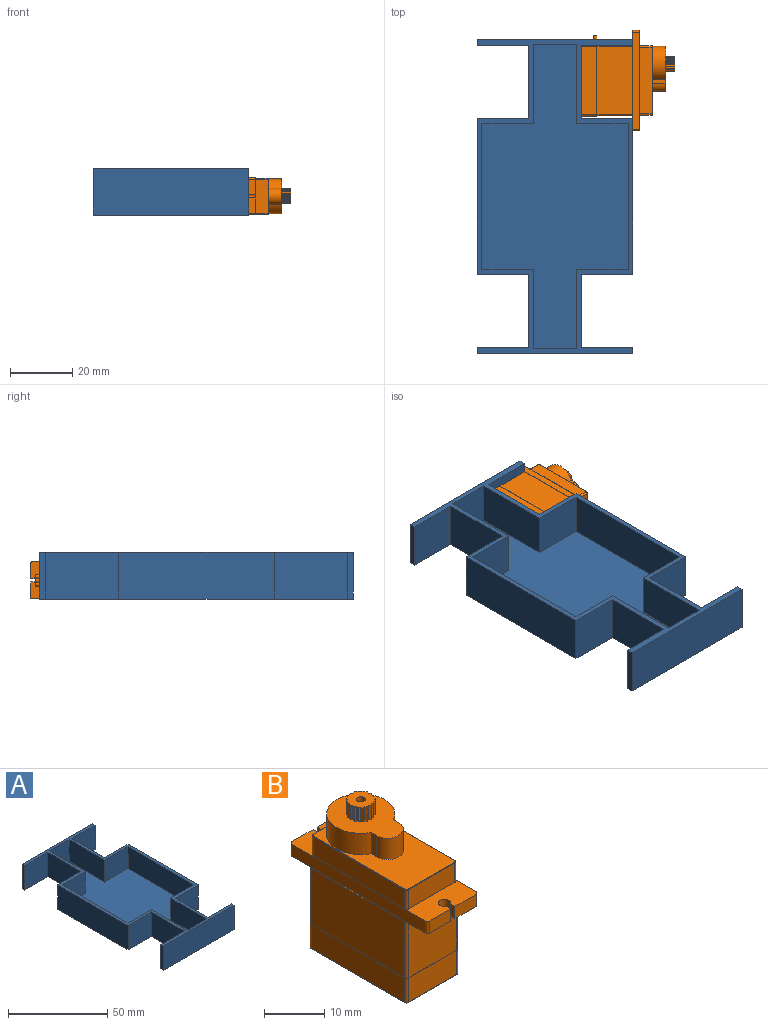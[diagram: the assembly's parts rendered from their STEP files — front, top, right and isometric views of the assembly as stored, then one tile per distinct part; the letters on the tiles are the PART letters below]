
ASSEMBLY  parts=2 mates=1
PART A: 35 faces, bbox 50x101x15 mm
  f0: plane 16.5x15mm, normal (0,1,0), area 247.5mm2, adj f1,f19,f20,f21
  f1: plane 50x15mm, normal (-1,0,0), area 750mm2, adj f0,f2,f20,f21
  f2: plane 16.5x15mm, normal (0,-1,0), area 247.5mm2, adj f1,f3,f20,f21
  f3: plane 23.5x15mm, normal (-1,0,0), area 352.5mm2, adj f2,f4,f20,f21
  f4: plane 16.5x15mm, normal (0,1,0), area 247.5mm2, adj f3,f5,f20,f21
  f5: plane 15x2mm, normal (-1,0,0), area 30mm2, adj f4,f6,f20,f21
  f6: plane 50x15mm, normal (0,-1,0), area 750mm2, adj f5,f7,f20,f21
  f7: plane 15x2mm, normal (1,0,0), area 30mm2, adj f6,f8,f20,f21
  f8: plane 16.5x15mm, normal (0,1,0), area 247.5mm2, adj f7,f9,f20,f21
  f9: plane 23.5x15mm, normal (1,0,0), area 352.5mm2, adj f8,f10,f20,f21
  f10: plane 16.5x15mm, normal (0,-1,0), area 247.5mm2, adj f9,f11,f20,f21
  f11: plane 50x15mm, normal (1,0,0), area 750mm2, adj f10,f12,f20,f21
  f12: plane 16.5x15mm, normal (0,1,0), area 247.5mm2, adj f11,f13,f20,f21
  f13: plane 23.5x15mm, normal (1,0,0), area 352.5mm2, adj f12,f14,f20,f21
  f14: plane 16.5x15mm, normal (0,-1,0), area 247.5mm2, adj f13,f15,f20,f21
  f15: plane 15x2mm, normal (1,0,0), area 30mm2, adj f14,f16,f20,f21
  f16: plane 50x15mm, normal (0,1,0), area 750mm2, adj f15,f17,f20,f21
  f17: plane 15x2mm, normal (-1,0,0), area 30mm2, adj f16,f18,f20,f21
  f18: plane 16.5x15mm, normal (0,-1,0), area 247.5mm2, adj f17,f19,f20,f21
  f19: plane 23.5x15mm, normal (-1,0,0), area 352.5mm2, adj f0,f18,f20,f21
  f20: plane 101x50mm, normal (0,0,1), area 576mm2, adj f0,f1,f2,f3,f4,f5,f6,f7
  f21: plane 101x50mm, normal (0,0,-1), area 3499mm2, adj f0,f1,f2,f3,f4,f5,f6,f7
  f22: plane 16.5x13.5mm, normal (0,-1,0), area 222.7mm2, adj f20,f23,f33,f34
  f23: plane 47x13.5mm, normal (1,0,0), area 634.5mm2, adj f20,f22,f24,f34
  f24: plane 16.5x13.5mm, normal (0,1,0), area 222.8mm2, adj f20,f23,f25,f34
  f25: plane 25.5x13.5mm, normal (1,0,0), area 344.2mm2, adj f20,f24,f26,f34
  f26: plane 14x13.5mm, normal (0,1,0), area 189mm2, adj f20,f25,f27,f34
  f27: plane 25.5x13.5mm, normal (-1,0,0), area 344.3mm2, adj f20,f26,f28,f34
  f28: plane 16.5x13.5mm, normal (0,1,0), area 222.8mm2, adj f20,f27,f29,f34
  f29: plane 47x13.5mm, normal (-1,0,0), area 634.5mm2, adj f20,f28,f30,f34
  f30: plane 16.5x13.5mm, normal (0,-1,0), area 222.7mm2, adj f20,f29,f31,f34
  f31: plane 25.5x13.5mm, normal (-1,0,0), area 344.3mm2, adj f20,f30,f32,f34
  f32: plane 14x13.5mm, normal (0,-1,0), area 189mm2, adj f20,f31,f33,f34
  f33: plane 25.5x13.5mm, normal (1,0,0), area 344.3mm2, adj f20,f22,f32,f34
  f34: plane 98x47mm, normal (0,0,1), area 2923mm2, adj f22,f23,f24,f25,f26,f27,f28,f29
PART B: 118 faces, bbox 12.4x32.3x30 mm
  f0: cylinder r=0.6mm len=3mm, axis (0,-1,0), area 11.3mm2, adj f15,f117
  f1: cylinder r=0.6mm len=3mm, axis (0,-1,0), area 11.3mm2, adj f15,f116
  f2: cylinder r=0.6mm len=3mm, axis (0,-1,0), area 11.3mm2, adj f15,f115
  f3: cylinder r=0.75mm len=2.9mm, axis (0,0,-1), area 13.7mm2, adj f97,f98
  f4: cylinder r=5.65mm len=11.3mm, axis (0,0,-1), area 129.4mm2, adj f6,f53,f54,f55
  f5: cylinder r=1mm len=2.45mm, axis (0,0,-1), area 12.8mm2, adj f7,f29,f42,f43
  f6: plane 14.55x11.3mm, normal (0,0,1), area 98.5mm2, adj f4,f54,f55,f56,f57,f58,f59,f60
  f7: plane 32.25x11.9mm, normal (0,0,1), area 111.1mm2, adj f5,f30,f31,f32,f33,f34,f35,f36
  f8: plane 22.41x0.15mm, normal (0,0,1), area 3.3mm2, adj f23,f24,f25,f39
  f9: plane 22.85x12.3mm, normal (0,0,1), area 4.1mm2, adj f10,f11,f12,f13,f14,f15,f16,f17
  f10: cylinder r=0.5mm len=4.9mm, axis (0,0,-1), area 3.8mm2, adj f9,f11,f17,f112
  f11: plane 11.3x4.9mm, normal (0,-1,0), area 55.4mm2, adj f9,f10,f12,f114
  f12: cylinder r=0.5mm len=4.9mm, axis (0,0,-1), area 3.8mm2, adj f9,f11,f13,f113
  f13: plane 21.85x4.9mm, normal (1,0,0), area 107.1mm2, adj f9,f12,f14,f111
  f14: cylinder r=0.5mm len=4.9mm, axis (0,0,-1), area 3.8mm2, adj f9,f13,f15,f109
  f15: plane 11.3x4.9mm, normal (0,1,0), area 52mm2, adj f0,f1,f2,f9,f14,f16,f107
  f16: cylinder r=0.5mm len=4.9mm, axis (0,0,-1), area 3.8mm2, adj f9,f15,f17,f108
  f17: plane 21.85x4.9mm, normal (-1,0,0), area 107.1mm2, adj f9,f10,f16,f110
  f18: plane 22.65x12.1mm, normal (0,0,-1), area 273.9mm2, adj f107,f108,f109,f110,f111,f112,f113,f114
  f19: cylinder r=0.5mm len=11.35mm, axis (0,0,-1), area 8.9mm2, adj f9,f20,f26,f27,f29
  f20: plane 21.7x11.35mm, normal (1,0,0), area 246.3mm2, adj f9,f19,f21,f27
  f21: cylinder r=0.5mm len=11.35mm, axis (0,0,-1), area 8.9mm2, adj f9,f20,f22,f27,f28
  f22: plane 11.35x11.2mm, normal (0,1,0), area 127.1mm2, adj f9,f21,f23,f28
  f23: cylinder r=0.5mm len=11.35mm, axis (0,0,-1), area 8.9mm2, adj f8,f9,f22,f24,f28
  f24: plane 21.7x11.35mm, normal (-1,0,0), area 246.3mm2, adj f8,f9,f23,f25
  f25: cylinder r=0.5mm len=11.35mm, axis (0,0,-1), area 8.9mm2, adj f8,f9,f24,f26,f29
  f26: plane 11.35x11.2mm, normal (0,-1,0), area 127.1mm2, adj f9,f19,f25,f29
  f27: plane 22.41x0.15mm, normal (0,0,1), area 3.3mm2, adj f19,f20,f21,f31
  f28: plane 11.9x4.92mm, normal (0,0,-1), area 52.6mm2, adj f21,f22,f23,f31,f32,f33,f34,f35
  f29: plane 11.9x4.92mm, normal (0,0,-1), area 52.6mm2, adj f5,f19,f25,f26,f30,f31,f39,f40
  f30: cylinder r=0.5mm len=2.45mm, axis (0,0,-1), area 1.9mm2, adj f7,f29,f31,f44
  f31: plane 31.25x2.45mm, normal (1,0,0), area 76.6mm2, adj f7,f27,f28,f29,f30,f32
  f32: cylinder r=0.5mm len=2.45mm, axis (0,0,-1), area 1.9mm2, adj f7,f28,f31,f33
  f33: plane 4.95x2.45mm, normal (0,1,0), area 12.1mm2, adj f7,f28,f32,f34
  f34: plane 2.45x1.13mm, normal (-1,0,0), area 2.8mm2, adj f7,f28,f33,f35
  f35: cylinder r=1mm len=2.45mm, axis (0,0,-1), area 12.8mm2, adj f7,f28,f34,f36
  f36: plane 2.45x1.13mm, normal (1,0,0), area 2.8mm2, adj f7,f28,f35,f37
  f37: plane 4.95x2.45mm, normal (0,1,0), area 12.1mm2, adj f7,f28,f36,f38
  f38: cylinder r=0.5mm len=2.45mm, axis (0,0,-1), area 1.9mm2, adj f7,f28,f37,f39
  f39: plane 31.25x2.45mm, normal (-1,0,0), area 76.6mm2, adj f7,f8,f28,f29,f38,f40
  f40: cylinder r=0.5mm len=2.45mm, axis (0,0,-1), area 1.9mm2, adj f7,f29,f39,f41
  f41: plane 4.95x2.45mm, normal (0,-1,0), area 12.1mm2, adj f7,f29,f40,f42
  f42: plane 2.45x1.13mm, normal (1,0,0), area 2.8mm2, adj f5,f7,f29,f41
  f43: plane 2.45x1.13mm, normal (-1,0,0), area 2.8mm2, adj f5,f7,f29,f44
  f44: plane 4.95x2.45mm, normal (0,-1,0), area 12.1mm2, adj f7,f29,f30,f43
  f45: cylinder r=0.5mm len=3.9mm, axis (0,0,-1), area 3.1mm2, adj f7,f46,f52,f99
  f46: plane 21.4x3.9mm, normal (1,0,0), area 83.5mm2, adj f7,f45,f47,f100
  f47: cylinder r=0.5mm len=3.9mm, axis (0,0,-1), area 3.1mm2, adj f7,f46,f48,f102
  f48: plane 10.8x3.9mm, normal (0,1,0), area 42.1mm2, adj f7,f47,f49,f104
  f49: cylinder r=0.5mm len=3.9mm, axis (0,0,-1), area 3.1mm2, adj f7,f48,f50,f106
  f50: plane 21.4x3.9mm, normal (-1,0,0), area 83.5mm2, adj f7,f49,f51,f105
  f51: cylinder r=0.5mm len=3.9mm, axis (0,0,-1), area 3.1mm2, adj f7,f50,f52,f103
  f52: plane 10.8x3.9mm, normal (0,-1,0), area 42.1mm2, adj f7,f45,f51,f101
  f53: plane 22.2x11.6mm, normal (0,0,1), area 142mm2, adj f4,f54,f55,f56,f99,f100,f101,f102
  f54: plane 4.3x1.28mm, normal (1,0,0), area 5.5mm2, adj f4,f6,f53,f56
  f55: plane 4.3x1.28mm, normal (-1,0,0), area 5.5mm2, adj f4,f6,f53,f56
  f56: cylinder r=2.6mm len=5.2mm, axis (0,0,-1), area 35.1mm2, adj f6,f53,f54,f55
  f57: plane 2.9x0.32mm, normal (0.63,0.78,0), area 1.2mm2, adj f6,f58,f96,f97
  f58: plane 2.9x0.42mm, normal (1,0.05,0), area 1.2mm2, adj f6,f57,f59,f97
  f59: plane 2.9x0.39mm, normal (0.36,0.93,0), area 1.2mm2, adj f6,f58,f60,f97
  f60: plane 2.9x0.39mm, normal (0.93,0.36,0), area 1.2mm2, adj f6,f59,f61,f97
  f61: plane 2.9x0.42mm, normal (0.05,1,0), area 1.2mm2, adj f6,f60,f62,f97
  f62: plane 2.9x0.32mm, normal (0.78,0.63,0), area 1.2mm2, adj f6,f61,f63,f97
  f63: plane 2.9x0.4mm, normal (-0.26,0.97,0), area 1.2mm2, adj f6,f62,f64,f97
  f64: plane 2.9x0.35mm, normal (0.55,0.84,0), area 1.2mm2, adj f6,f63,f65,f97
  f65: plane 2.9x0.35mm, normal (-0.55,0.84,0), area 1.2mm2, adj f6,f64,f66,f97
  f66: plane 2.9x0.4mm, normal (0.26,0.97,0), area 1.2mm2, adj f6,f65,f67,f97
  f67: plane 2.9x0.32mm, normal (-0.78,0.63,0), area 1.2mm2, adj f6,f66,f68,f97
  f68: plane 2.9x0.42mm, normal (-0.05,1,0), area 1.2mm2, adj f6,f67,f69,f97
  f69: plane 2.9x0.39mm, normal (-0.93,0.36,0), area 1.2mm2, adj f6,f68,f70,f97
  f70: plane 2.9x0.39mm, normal (-0.36,0.93,0), area 1.2mm2, adj f6,f69,f71,f97
  f71: plane 2.9x0.42mm, normal (-1,0.05,0), area 1.2mm2, adj f6,f70,f72,f97
  f72: plane 2.9x0.32mm, normal (-0.63,0.78,0), area 1.2mm2, adj f6,f71,f73,f97
  f73: plane 2.9x0.4mm, normal (-0.97,-0.26,0), area 1.2mm2, adj f6,f72,f74,f97
  f74: plane 2.9x0.35mm, normal (-0.84,0.55,0), area 1.2mm2, adj f6,f73,f75,f97
  f75: plane 2.9x0.35mm, normal (-0.84,-0.55,0), area 1.2mm2, adj f6,f74,f76,f97
  f76: plane 2.9x0.4mm, normal (-0.97,0.26,0), area 1.2mm2, adj f6,f75,f77,f97
  f77: plane 2.9x0.32mm, normal (-0.63,-0.78,0), area 1.2mm2, adj f6,f76,f78,f97
  f78: plane 2.9x0.42mm, normal (-1,-0.05,0), area 1.2mm2, adj f6,f77,f79,f97
  f79: plane 2.9x0.39mm, normal (-0.36,-0.93,0), area 1.2mm2, adj f6,f78,f80,f97
  f80: plane 2.9x0.39mm, normal (-0.93,-0.36,0), area 1.2mm2, adj f6,f79,f81,f97
  f81: plane 2.9x0.42mm, normal (-0.05,-1,0), area 1.2mm2, adj f6,f80,f82,f97
  f82: plane 2.9x0.32mm, normal (-0.78,-0.63,0), area 1.2mm2, adj f6,f81,f83,f97
  f83: plane 2.9x0.4mm, normal (0.26,-0.97,0), area 1.2mm2, adj f6,f82,f84,f97
  f84: plane 2.9x0.35mm, normal (-0.55,-0.84,0), area 1.2mm2, adj f6,f83,f85,f97
  f85: plane 2.9x0.35mm, normal (0.55,-0.84,0), area 1.2mm2, adj f6,f84,f86,f97
  f86: plane 2.9x0.4mm, normal (-0.26,-0.97,0), area 1.2mm2, adj f6,f85,f87,f97
  f87: plane 2.9x0.32mm, normal (0.78,-0.63,0), area 1.2mm2, adj f6,f86,f88,f97
  f88: plane 2.9x0.42mm, normal (0.05,-1,0), area 1.2mm2, adj f6,f87,f89,f97
  f89: plane 2.9x0.39mm, normal (0.93,-0.36,0), area 1.2mm2, adj f6,f88,f90,f97
  f90: plane 2.9x0.39mm, normal (0.36,-0.93,0), area 1.2mm2, adj f6,f89,f91,f97
  f91: plane 2.9x0.42mm, normal (1,-0.05,0), area 1.2mm2, adj f6,f90,f92,f97
  f92: plane 2.9x0.32mm, normal (0.63,-0.78,0), area 1.2mm2, adj f6,f91,f93,f97
  f93: plane 2.9x0.4mm, normal (0.97,0.26,0), area 1.2mm2, adj f6,f92,f94,f97
  f94: plane 2.9x0.35mm, normal (0.84,-0.55,0), area 1.2mm2, adj f6,f93,f95,f97
  f95: plane 2.9x0.35mm, normal (0.84,0.55,0), area 1.2mm2, adj f6,f94,f96,f97
  f96: plane 2.9x0.4mm, normal (0.97,-0.26,0), area 1.2mm2, adj f6,f57,f95,f97
  f97: plane 4.85x4.85mm, normal (0,0,1), area 15.1mm2, adj f3,f57,f58,f59,f60,f61,f62,f63
  f98: plane 1.5x1.5mm, normal (0,0,1), area 1.8mm2, adj f3
  f99: torus R=0.4mm, axis (0,0,1), area 0.1mm2, adj f45,f53,f100,f101
  f100: cylinder r=0.1mm len=21.4mm, axis (0,-1,0), area 3.4mm2, adj f46,f53,f99,f102
  f101: cylinder r=0.1mm len=10.8mm, axis (-1,0,0), area 1.7mm2, adj f52,f53,f99,f103
  f102: torus R=0.4mm, axis (0,0,1), area 0.1mm2, adj f47,f53,f100,f104
  f103: torus R=0.4mm, axis (0,0,1), area 0.1mm2, adj f51,f53,f101,f105
  f104: cylinder r=0.1mm len=10.8mm, axis (1,0,0), area 1.7mm2, adj f48,f53,f102,f106
  f105: cylinder r=0.1mm len=21.4mm, axis (0,1,0), area 3.4mm2, adj f50,f53,f103,f106
  f106: torus R=0.4mm, axis (0,0,1), area 0.1mm2, adj f49,f53,f104,f105
  f107: cylinder r=0.1mm len=11.3mm, axis (1,0,0), area 1.8mm2, adj f15,f18,f108,f109
  f108: torus R=0.4mm, axis (0,0,-1), area 0.1mm2, adj f16,f18,f107,f110
  f109: torus R=0.4mm, axis (0,0,-1), area 0.1mm2, adj f14,f18,f107,f111
  f110: cylinder r=0.1mm len=21.85mm, axis (0,1,0), area 3.4mm2, adj f17,f18,f108,f112
  f111: cylinder r=0.1mm len=21.85mm, axis (0,-1,0), area 3.4mm2, adj f13,f18,f109,f113
  f112: torus R=0.4mm, axis (0,0,-1), area 0.1mm2, adj f10,f18,f110,f114
  f113: torus R=0.4mm, axis (0,0,-1), area 0.1mm2, adj f12,f18,f111,f114
  f114: cylinder r=0.1mm len=11.3mm, axis (-1,0,0), area 1.8mm2, adj f11,f18,f112,f113
  f115: plane 1.2x1.2mm, normal (0,1,0), area 1.1mm2, adj f2
  f116: plane 1.2x1.2mm, normal (0,1,0), area 1.1mm2, adj f1
  f117: plane 1.2x1.2mm, normal (0,1,0), area 1.1mm2, adj f0
PLACE A at identity
PLACE B rot(axis=(0,1,0),90deg) t=(8.5,37.25,6)mm
MATE parallel A.f13 <-> B.f18  axis (1,0,0) through (8.5,36.75,7.5)mm
